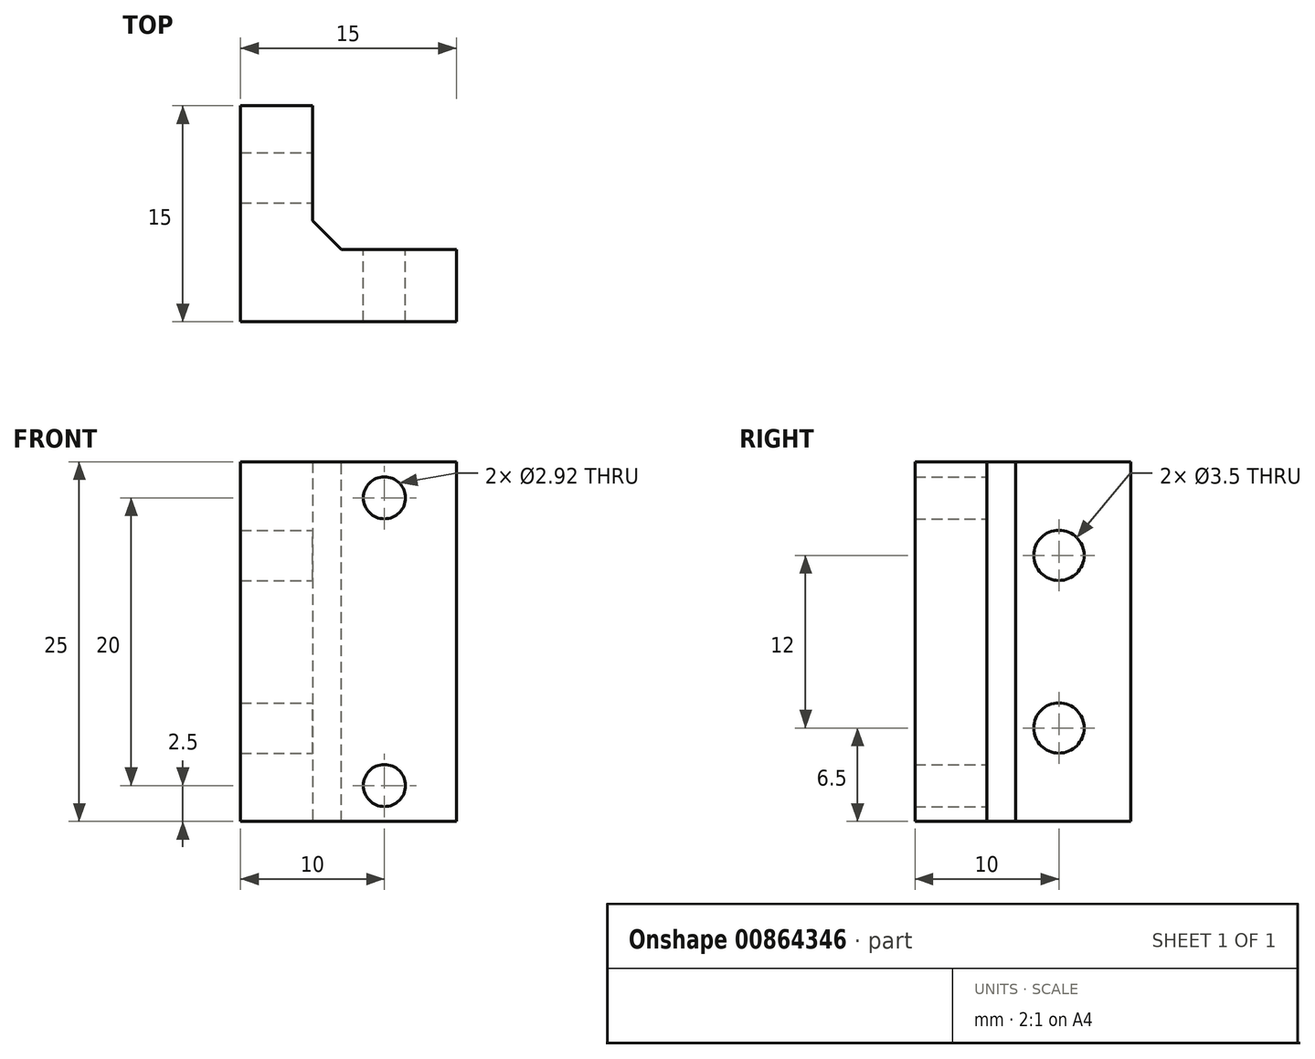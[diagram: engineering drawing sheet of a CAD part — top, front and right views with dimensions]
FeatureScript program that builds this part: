
annotation { "Feature Type Name" : "Feature", "Feature Type Description" : "" }
export const myFeature = defineFeature(function(context is Context, id is Id, definition is map)
    precondition{}
    {
        {
            var Q0;
            Q0=qCreatedBy(makeId("Top.planeOp"),FACE);
            var sketch = newSketch(context, id + "F0", { "sketchPlane" : qUnion([Q0])});
            skLineSegment(sketch, "E0", {"start": v(0, 0) * mm, "end": v(0, 15) * mm});
            skLineSegment(sketch, "E1", {"start": v(0, 15) * mm, "end": v(5, 15) * mm});
            skLineSegment(sketch, "E2", {"start": v(5, 15) * mm, "end": v(5, 5) * mm});
            skLineSegment(sketch, "E3", {"start": v(5, 5) * mm, "end": v(15, 5) * mm});
            skLineSegment(sketch, "E4", {"start": v(15, 5) * mm, "end": v(15, 0) * mm});
            skLineSegment(sketch, "E5", {"start": v(15, 0) * mm, "end": v(0, 0) * mm});
            skSolve(sketch);
        }
        {
            var Q0;
            Q0 = qSketchRegion(id + "F0", true);
            extrude(context, id + "F1", {"entities" : qUnion([Q0]), "depth" : 25 * mm, "offsetDistance" : 25 * mm});
        }
        {
            var Q0;
            Q0=makeQuery(id+"F1.opExtrude","SWEPT_FACE",FACE,{"disambiguationData":[OSD([sQuery(id+"F0.wireOp",EDGE,"E2")])]});
            var sketch = newSketch(context, id + "F2", { "sketchPlane" : qUnion([Q0])});
            skLineSegment(sketch, "E6", {"start": v(10, 0) * mm, "end": v(10, 25) * mm, "construction": true});
            skCircle(sketch, "E7", {"center": v(10, 6.5) * mm, "radius": 1.75 * mm});
            skLineSegment(sketch, "E8", {"start": v(10, 12.5) * mm, "end": v(15, 12.5) * mm, "construction": true});
            skCircle(sketch, "E9.MirrorC", {"center": v(10, 18.5) * mm, "radius": 1.75 * mm});
            skSolve(sketch);
        }
        {
            var Q0;
            Q0 = qSketchRegion(id + "F2", true);
            extrude(context, id + "F3", {"entities" : qUnion([Q0]), "operationType" : NewBodyOperationType.REMOVE, "oppositeDirection" : true, "depth" : 25 * mm, "offsetDistance" : 25 * mm});
        }
        {
            var Q0;
            Q0=makeQuery(id+"F1.opExtrude","SWEPT_FACE",FACE,{"disambiguationData":[OSD([sQuery(id+"F0.wireOp",EDGE,"E3")])]});
            var sketch = newSketch(context, id + "F4", { "sketchPlane" : qUnion([Q0])});
            skCircle(sketch, "E10", {"center": v(-10, 2.5) * mm, "radius": 1.46 * mm});
            skPoint(sketch, "E10.centerSnap0", {"position": v(-10, 0) * mm});
            skLineSegment(sketch, "E11", {"start": v(-15, 12.5) * mm, "end": v(-5, 12.5) * mm, "construction": true});
            skCircle(sketch, "E12.MirrorC", {"center": v(-10, 22.5) * mm, "radius": 1.46 * mm});
            skSolve(sketch);
        }
        {
            var Q0;
            Q0 = qSketchRegion(id + "F4", true);
            extrude(context, id + "F5", {"entities" : qUnion([Q0]), "operationType" : NewBodyOperationType.REMOVE, "oppositeDirection" : true, "depth" : 25 * mm, "offsetDistance" : 25 * mm});
        }
        {
            var Q0;
            Q0=makeQuery(id+"F1.opExtrude","SWEPT_EDGE",EDGE,{"disambiguationData":[OSD([sQuery(id+"F0.wireOp",EDGE,"E2"),sQuery(id+"F0.wireOp",EDGE,"E3")])]});
            chamfer(context, id + "F6", {"entities" : qUnion([Q0]), "width" : 2 * mm, "tangentPropagation" : true});
        }
    });
